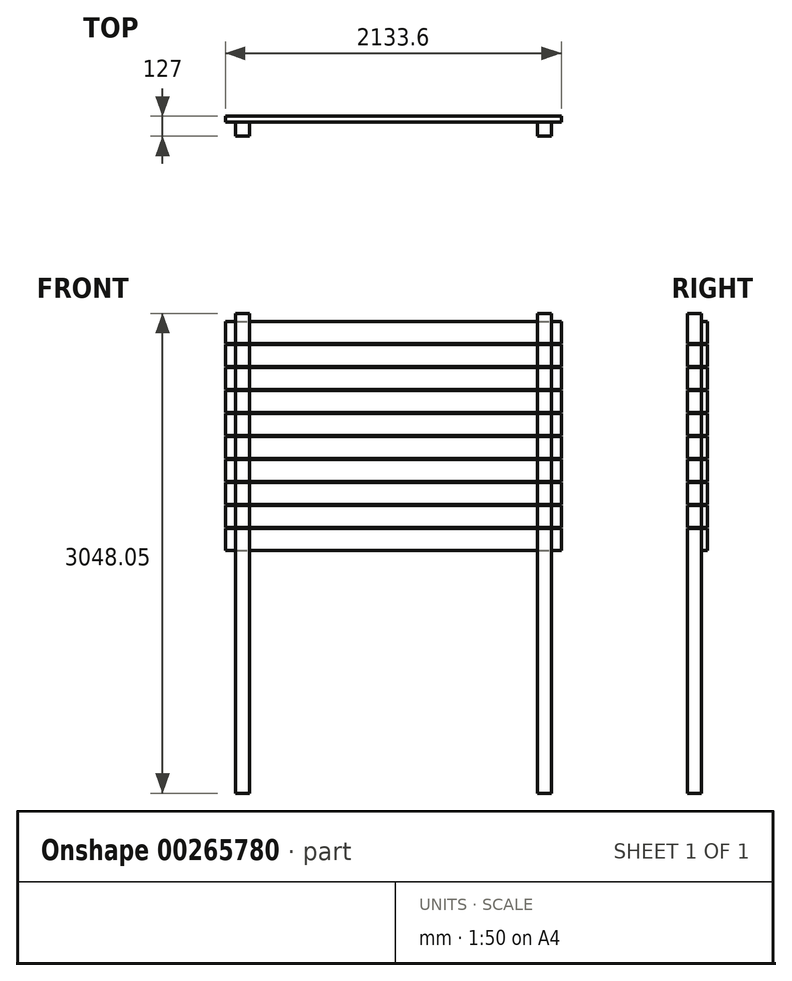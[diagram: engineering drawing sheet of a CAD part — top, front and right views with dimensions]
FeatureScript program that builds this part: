
annotation { "Feature Type Name" : "Feature", "Feature Type Description" : "" }
export const myFeature = defineFeature(function(context is Context, id is Id, definition is map)
    precondition{}
    {
        {
            var Q0;
            Q0=qCreatedBy(makeId("Front.planeOp"),FACE);
            var sketch = newSketch(context, id + "F0", { "sketchPlane" : qUnion([Q0])});
            skLineSegment(sketch, "E0.bottom", {"start": v(-158.67, 1590.1) * mm, "end": v(-69.77, 1590.1) * mm});
            skLineSegment(sketch, "E0.top", {"start": v(-158.67, -1457.9) * mm, "end": v(-69.77, -1457.9) * mm});
            skLineSegment(sketch, "E0.left", {"start": v(-158.67, 1590.1) * mm, "end": v(-158.67, -1457.9) * mm});
            skLineSegment(sketch, "E0.right", {"start": v(-69.77, 1590.1) * mm, "end": v(-69.77, -1457.9) * mm});
            skLineSegment(sketch, "E1.bottom", {"start": v(1759.03, 1590.04) * mm, "end": v(1847.93, 1590.04) * mm});
            skLineSegment(sketch, "E1.top", {"start": v(1759.03, -1457.96) * mm, "end": v(1847.93, -1457.96) * mm});
            skLineSegment(sketch, "E1.left", {"start": v(1759.03, 1590.04) * mm, "end": v(1759.03, -1457.96) * mm});
            skLineSegment(sketch, "E1.right", {"start": v(1847.93, 1590.04) * mm, "end": v(1847.93, -1457.96) * mm});
            skLineSegment(sketch, "E2", {"start": v(-615.63, -543.5) * mm, "end": v(2237.65, -543.5) * mm});
            skLineSegment(sketch, "E3.bottom", {"start": v(-222.17, 1539.46) * mm, "end": v(1911.43, 1539.46) * mm});
            skLineSegment(sketch, "E3.top", {"start": v(-222.17, 1399.76) * mm, "end": v(1911.43, 1399.76) * mm});
            skLineSegment(sketch, "E3.left", {"start": v(-222.17, 1539.46) * mm, "end": v(-222.17, 1399.76) * mm});
            skLineSegment(sketch, "E3.right", {"start": v(1911.43, 1539.46) * mm, "end": v(1911.43, 1399.76) * mm});
            skLineSegment(sketch, "E4.0.1.0", {"start": v(-222.17, 1393.41) * mm, "end": v(-222.17, 1253.71) * mm});
            skLineSegment(sketch, "E4.0.1.1", {"start": v(-222.17, 1393.41) * mm, "end": v(1911.43, 1393.41) * mm});
            skLineSegment(sketch, "E4.0.1.2", {"start": v(-222.17, 1253.71) * mm, "end": v(1911.43, 1253.71) * mm});
            skLineSegment(sketch, "E4.0.1.3", {"start": v(1911.43, 1393.41) * mm, "end": v(1911.43, 1253.71) * mm});
            skLineSegment(sketch, "E4.0.2.0", {"start": v(-222.17, 1247.36) * mm, "end": v(-222.17, 1107.66) * mm});
            skLineSegment(sketch, "E4.0.2.1", {"start": v(-222.17, 1247.36) * mm, "end": v(1911.43, 1247.36) * mm});
            skLineSegment(sketch, "E4.0.2.2", {"start": v(-222.17, 1107.66) * mm, "end": v(1911.43, 1107.66) * mm});
            skLineSegment(sketch, "E4.0.2.3", {"start": v(1911.43, 1247.36) * mm, "end": v(1911.43, 1107.66) * mm});
            skLineSegment(sketch, "E4.0.3.0", {"start": v(-222.17, 1101.31) * mm, "end": v(-222.17, 961.61) * mm});
            skLineSegment(sketch, "E4.0.3.1", {"start": v(-222.17, 1101.31) * mm, "end": v(1911.43, 1101.31) * mm});
            skLineSegment(sketch, "E4.0.3.2", {"start": v(-222.17, 961.61) * mm, "end": v(1911.43, 961.61) * mm});
            skLineSegment(sketch, "E4.0.3.3", {"start": v(1911.43, 1101.31) * mm, "end": v(1911.43, 961.61) * mm});
            skLineSegment(sketch, "E4.0.4.0", {"start": v(-222.17, 955.26) * mm, "end": v(-222.17, 815.56) * mm});
            skLineSegment(sketch, "E4.0.4.1", {"start": v(-222.17, 955.26) * mm, "end": v(1911.43, 955.26) * mm});
            skLineSegment(sketch, "E4.0.4.2", {"start": v(-222.17, 815.56) * mm, "end": v(1911.43, 815.56) * mm});
            skLineSegment(sketch, "E4.0.4.3", {"start": v(1911.43, 955.26) * mm, "end": v(1911.43, 815.56) * mm});
            skLineSegment(sketch, "E4.0.5.0", {"start": v(-222.17, 809.21) * mm, "end": v(-222.17, 669.51) * mm});
            skLineSegment(sketch, "E4.0.5.1", {"start": v(-222.17, 809.21) * mm, "end": v(1911.43, 809.21) * mm});
            skLineSegment(sketch, "E4.0.5.2", {"start": v(-222.17, 669.51) * mm, "end": v(1911.43, 669.51) * mm});
            skLineSegment(sketch, "E4.0.5.3", {"start": v(1911.43, 809.21) * mm, "end": v(1911.43, 669.51) * mm});
            skLineSegment(sketch, "E4.0.6.0", {"start": v(-222.17, 663.16) * mm, "end": v(-222.17, 523.46) * mm});
            skLineSegment(sketch, "E4.0.6.1", {"start": v(-222.17, 663.16) * mm, "end": v(1911.43, 663.16) * mm});
            skLineSegment(sketch, "E4.0.6.2", {"start": v(-222.17, 523.46) * mm, "end": v(1911.43, 523.46) * mm});
            skLineSegment(sketch, "E4.0.6.3", {"start": v(1911.43, 663.16) * mm, "end": v(1911.43, 523.46) * mm});
            skLineSegment(sketch, "E4.0.7.0", {"start": v(-222.17, 517.11) * mm, "end": v(-222.17, 377.41) * mm});
            skLineSegment(sketch, "E4.0.7.1", {"start": v(-222.17, 517.11) * mm, "end": v(1911.43, 517.11) * mm});
            skLineSegment(sketch, "E4.0.7.2", {"start": v(-222.17, 377.41) * mm, "end": v(1911.43, 377.41) * mm});
            skLineSegment(sketch, "E4.0.7.3", {"start": v(1911.43, 517.11) * mm, "end": v(1911.43, 377.41) * mm});
            skLineSegment(sketch, "E4.0.8.0", {"start": v(-222.17, 371.06) * mm, "end": v(-222.17, 231.36) * mm});
            skLineSegment(sketch, "E4.0.8.1", {"start": v(-222.17, 371.06) * mm, "end": v(1911.43, 371.06) * mm});
            skLineSegment(sketch, "E4.0.8.2", {"start": v(-222.17, 231.36) * mm, "end": v(1911.43, 231.36) * mm});
            skLineSegment(sketch, "E4.0.8.3", {"start": v(1911.43, 371.06) * mm, "end": v(1911.43, 231.36) * mm});
            skLineSegment(sketch, "E4.0.9.0", {"start": v(-222.17, 225.01) * mm, "end": v(-222.17, 85.31) * mm});
            skLineSegment(sketch, "E4.0.9.1", {"start": v(-222.17, 225.01) * mm, "end": v(1911.43, 225.01) * mm});
            skLineSegment(sketch, "E4.0.9.2", {"start": v(-222.17, 85.31) * mm, "end": v(1911.43, 85.31) * mm});
            skLineSegment(sketch, "E4.0.9.3", {"start": v(1911.43, 225.01) * mm, "end": v(1911.43, 85.31) * mm});
            skLineSegment(sketch, "E4.direction1", {"start": v(-222.17, 1399.76) * mm, "end": v(-219.63, 1399.76) * mm, "construction": true});
            skLineSegment(sketch, "E4.direction2", {"start": v(-222.17, 1399.76) * mm, "end": v(-222.17, 1253.71) * mm, "construction": true});
            skSolve(sketch);
        }
        {
            var Q0;
            {var subQ0=sQuery(id+"F0.wireOp",EDGE,"E0.top");Q0=makeQuery(id+"F0.imprint","IMPRINT",FACE,{"disambiguationData":[TD([[makeQuery(id+"F0.imprint","IMPRINT",EDGE,{"derivedFrom":subQ0}),1.0]])]});}
            var Q1;
            {var subQ0=sQuery(id+"F0.wireOp",EDGE,"E2");var subQ1=sQuery(id+"F0.wireOp",EDGE,"E0.left");var subQ2=makeQuery(id+"F0.imprint","INTERSECT",VERTEX,{"derivedFrom":[subQ1,subQ0]});Q1=makeQuery(id+"F0.imprint","IMPRINT",FACE,{"disambiguationData":[TD([[makeQuery(id+"F0.imprint","IMPRINT",EDGE,{"disambiguationData":[TD([[subQ2,1.0]])],"derivedFrom":subQ1}),1.0]])]});}
            var Q2;
            {var subQ0=sQuery(id+"F0.wireOp",EDGE,"E4.0.9.1");var subQ1=sQuery(id+"F0.wireOp",EDGE,"E0.left");var subQ2=makeQuery(id+"F0.imprint","INTERSECT",VERTEX,{"derivedFrom":[subQ1,subQ0]});Q2=makeQuery(id+"F0.imprint","IMPRINT",FACE,{"disambiguationData":[TD([[makeQuery(id+"F0.imprint","IMPRINT",EDGE,{"disambiguationData":[TD([[subQ2,-1.0]])],"derivedFrom":subQ1}),1.0]])]});}
            var Q3;
            {var subQ0=sQuery(id+"F0.wireOp",EDGE,"E4.0.8.1");var subQ1=sQuery(id+"F0.wireOp",EDGE,"E0.left");var subQ2=makeQuery(id+"F0.imprint","INTERSECT",VERTEX,{"derivedFrom":[subQ1,subQ0]});Q3=makeQuery(id+"F0.imprint","IMPRINT",FACE,{"disambiguationData":[TD([[makeQuery(id+"F0.imprint","IMPRINT",EDGE,{"disambiguationData":[TD([[subQ2,-1.0]])],"derivedFrom":subQ1}),1.0]])]});}
            var Q4;
            {var subQ0=sQuery(id+"F0.wireOp",EDGE,"E4.0.7.1");var subQ1=sQuery(id+"F0.wireOp",EDGE,"E0.left");var subQ2=makeQuery(id+"F0.imprint","INTERSECT",VERTEX,{"derivedFrom":[subQ1,subQ0]});Q4=makeQuery(id+"F0.imprint","IMPRINT",FACE,{"disambiguationData":[TD([[makeQuery(id+"F0.imprint","IMPRINT",EDGE,{"disambiguationData":[TD([[subQ2,-1.0]])],"derivedFrom":subQ1}),1.0]])]});}
            var Q5;
            {var subQ0=sQuery(id+"F0.wireOp",EDGE,"E4.0.6.1");var subQ1=sQuery(id+"F0.wireOp",EDGE,"E0.left");var subQ2=makeQuery(id+"F0.imprint","INTERSECT",VERTEX,{"derivedFrom":[subQ1,subQ0]});Q5=makeQuery(id+"F0.imprint","IMPRINT",FACE,{"disambiguationData":[TD([[makeQuery(id+"F0.imprint","IMPRINT",EDGE,{"disambiguationData":[TD([[subQ2,-1.0]])],"derivedFrom":subQ1}),1.0]])]});}
            var Q6;
            {var subQ0=sQuery(id+"F0.wireOp",EDGE,"E4.0.5.1");var subQ1=sQuery(id+"F0.wireOp",EDGE,"E0.left");var subQ2=makeQuery(id+"F0.imprint","INTERSECT",VERTEX,{"derivedFrom":[subQ1,subQ0]});Q6=makeQuery(id+"F0.imprint","IMPRINT",FACE,{"disambiguationData":[TD([[makeQuery(id+"F0.imprint","IMPRINT",EDGE,{"disambiguationData":[TD([[subQ2,-1.0]])],"derivedFrom":subQ1}),1.0]])]});}
            var Q7;
            {var subQ0=sQuery(id+"F0.wireOp",EDGE,"E4.0.4.1");var subQ1=sQuery(id+"F0.wireOp",EDGE,"E0.left");var subQ2=makeQuery(id+"F0.imprint","INTERSECT",VERTEX,{"derivedFrom":[subQ1,subQ0]});Q7=makeQuery(id+"F0.imprint","IMPRINT",FACE,{"disambiguationData":[TD([[makeQuery(id+"F0.imprint","IMPRINT",EDGE,{"disambiguationData":[TD([[subQ2,-1.0]])],"derivedFrom":subQ1}),1.0]])]});}
            var Q8;
            {var subQ0=sQuery(id+"F0.wireOp",EDGE,"E4.0.3.1");var subQ1=sQuery(id+"F0.wireOp",EDGE,"E0.left");var subQ2=makeQuery(id+"F0.imprint","INTERSECT",VERTEX,{"derivedFrom":[subQ1,subQ0]});Q8=makeQuery(id+"F0.imprint","IMPRINT",FACE,{"disambiguationData":[TD([[makeQuery(id+"F0.imprint","IMPRINT",EDGE,{"disambiguationData":[TD([[subQ2,-1.0]])],"derivedFrom":subQ1}),1.0]])]});}
            var Q9;
            {var subQ0=sQuery(id+"F0.wireOp",EDGE,"E4.0.2.1");var subQ1=sQuery(id+"F0.wireOp",EDGE,"E0.left");var subQ2=makeQuery(id+"F0.imprint","INTERSECT",VERTEX,{"derivedFrom":[subQ1,subQ0]});Q9=makeQuery(id+"F0.imprint","IMPRINT",FACE,{"disambiguationData":[TD([[makeQuery(id+"F0.imprint","IMPRINT",EDGE,{"disambiguationData":[TD([[subQ2,-1.0]])],"derivedFrom":subQ1}),1.0]])]});}
            var Q10;
            {var subQ0=sQuery(id+"F0.wireOp",EDGE,"E4.0.1.1");var subQ1=sQuery(id+"F0.wireOp",EDGE,"E0.left");var subQ2=makeQuery(id+"F0.imprint","INTERSECT",VERTEX,{"derivedFrom":[subQ1,subQ0]});Q10=makeQuery(id+"F0.imprint","IMPRINT",FACE,{"disambiguationData":[TD([[makeQuery(id+"F0.imprint","IMPRINT",EDGE,{"disambiguationData":[TD([[subQ2,-1.0]])],"derivedFrom":subQ1}),1.0]])]});}
            var Q11;
            {var subQ0=sQuery(id+"F0.wireOp",EDGE,"E3.bottom");var subQ1=sQuery(id+"F0.wireOp",EDGE,"E0.left");var subQ2=makeQuery(id+"F0.imprint","INTERSECT",VERTEX,{"derivedFrom":[subQ1,subQ0]});Q11=makeQuery(id+"F0.imprint","IMPRINT",FACE,{"disambiguationData":[TD([[makeQuery(id+"F0.imprint","IMPRINT",EDGE,{"disambiguationData":[TD([[subQ2,-1.0]])],"derivedFrom":subQ1}),1.0]])]});}
            var Q12;
            {var subQ0=sQuery(id+"F0.wireOp",EDGE,"E0.bottom");Q12=makeQuery(id+"F0.imprint","IMPRINT",FACE,{"disambiguationData":[TD([[makeQuery(id+"F0.imprint","IMPRINT",EDGE,{"derivedFrom":subQ0}),-1.0]])]});}
            var Q13;
            {var subQ0=sQuery(id+"F0.wireOp",EDGE,"E1.bottom");Q13=makeQuery(id+"F0.imprint","IMPRINT",FACE,{"disambiguationData":[TD([[makeQuery(id+"F0.imprint","IMPRINT",EDGE,{"derivedFrom":subQ0}),-1.0]])]});}
            var Q14;
            {var subQ0=sQuery(id+"F0.wireOp",EDGE,"E3.bottom");var subQ1=sQuery(id+"F0.wireOp",EDGE,"E1.left");var subQ2=makeQuery(id+"F0.imprint","INTERSECT",VERTEX,{"derivedFrom":[subQ1,subQ0]});Q14=makeQuery(id+"F0.imprint","IMPRINT",FACE,{"disambiguationData":[TD([[makeQuery(id+"F0.imprint","IMPRINT",EDGE,{"disambiguationData":[TD([[subQ2,-1.0]])],"derivedFrom":subQ1}),1.0]])]});}
            var Q15;
            {var subQ0=sQuery(id+"F0.wireOp",EDGE,"E4.0.1.1");var subQ1=sQuery(id+"F0.wireOp",EDGE,"E1.left");var subQ2=makeQuery(id+"F0.imprint","INTERSECT",VERTEX,{"derivedFrom":[subQ1,subQ0]});Q15=makeQuery(id+"F0.imprint","IMPRINT",FACE,{"disambiguationData":[TD([[makeQuery(id+"F0.imprint","IMPRINT",EDGE,{"disambiguationData":[TD([[subQ2,-1.0]])],"derivedFrom":subQ1}),1.0]])]});}
            var Q16;
            {var subQ0=sQuery(id+"F0.wireOp",EDGE,"E4.0.2.1");var subQ1=sQuery(id+"F0.wireOp",EDGE,"E1.left");var subQ2=makeQuery(id+"F0.imprint","INTERSECT",VERTEX,{"derivedFrom":[subQ1,subQ0]});Q16=makeQuery(id+"F0.imprint","IMPRINT",FACE,{"disambiguationData":[TD([[makeQuery(id+"F0.imprint","IMPRINT",EDGE,{"disambiguationData":[TD([[subQ2,-1.0]])],"derivedFrom":subQ1}),1.0]])]});}
            var Q17;
            {var subQ0=sQuery(id+"F0.wireOp",EDGE,"E4.0.3.1");var subQ1=sQuery(id+"F0.wireOp",EDGE,"E1.left");var subQ2=makeQuery(id+"F0.imprint","INTERSECT",VERTEX,{"derivedFrom":[subQ1,subQ0]});Q17=makeQuery(id+"F0.imprint","IMPRINT",FACE,{"disambiguationData":[TD([[makeQuery(id+"F0.imprint","IMPRINT",EDGE,{"disambiguationData":[TD([[subQ2,-1.0]])],"derivedFrom":subQ1}),1.0]])]});}
            var Q18;
            {var subQ0=sQuery(id+"F0.wireOp",EDGE,"E4.0.4.1");var subQ1=sQuery(id+"F0.wireOp",EDGE,"E1.left");var subQ2=makeQuery(id+"F0.imprint","INTERSECT",VERTEX,{"derivedFrom":[subQ1,subQ0]});Q18=makeQuery(id+"F0.imprint","IMPRINT",FACE,{"disambiguationData":[TD([[makeQuery(id+"F0.imprint","IMPRINT",EDGE,{"disambiguationData":[TD([[subQ2,-1.0]])],"derivedFrom":subQ1}),1.0]])]});}
            var Q19;
            {var subQ0=sQuery(id+"F0.wireOp",EDGE,"E4.0.5.1");var subQ1=sQuery(id+"F0.wireOp",EDGE,"E1.left");var subQ2=makeQuery(id+"F0.imprint","INTERSECT",VERTEX,{"derivedFrom":[subQ1,subQ0]});Q19=makeQuery(id+"F0.imprint","IMPRINT",FACE,{"disambiguationData":[TD([[makeQuery(id+"F0.imprint","IMPRINT",EDGE,{"disambiguationData":[TD([[subQ2,-1.0]])],"derivedFrom":subQ1}),1.0]])]});}
            var Q20;
            {var subQ0=sQuery(id+"F0.wireOp",EDGE,"E4.0.6.1");var subQ1=sQuery(id+"F0.wireOp",EDGE,"E1.left");var subQ2=makeQuery(id+"F0.imprint","INTERSECT",VERTEX,{"derivedFrom":[subQ1,subQ0]});Q20=makeQuery(id+"F0.imprint","IMPRINT",FACE,{"disambiguationData":[TD([[makeQuery(id+"F0.imprint","IMPRINT",EDGE,{"disambiguationData":[TD([[subQ2,-1.0]])],"derivedFrom":subQ1}),1.0]])]});}
            var Q21;
            {var subQ0=sQuery(id+"F0.wireOp",EDGE,"E4.0.7.1");var subQ1=sQuery(id+"F0.wireOp",EDGE,"E1.left");var subQ2=makeQuery(id+"F0.imprint","INTERSECT",VERTEX,{"derivedFrom":[subQ1,subQ0]});Q21=makeQuery(id+"F0.imprint","IMPRINT",FACE,{"disambiguationData":[TD([[makeQuery(id+"F0.imprint","IMPRINT",EDGE,{"disambiguationData":[TD([[subQ2,-1.0]])],"derivedFrom":subQ1}),1.0]])]});}
            var Q22;
            {var subQ0=sQuery(id+"F0.wireOp",EDGE,"E4.0.8.1");var subQ1=sQuery(id+"F0.wireOp",EDGE,"E1.left");var subQ2=makeQuery(id+"F0.imprint","INTERSECT",VERTEX,{"derivedFrom":[subQ1,subQ0]});Q22=makeQuery(id+"F0.imprint","IMPRINT",FACE,{"disambiguationData":[TD([[makeQuery(id+"F0.imprint","IMPRINT",EDGE,{"disambiguationData":[TD([[subQ2,-1.0]])],"derivedFrom":subQ1}),1.0]])]});}
            var Q23;
            {var subQ0=sQuery(id+"F0.wireOp",EDGE,"E4.0.9.1");var subQ1=sQuery(id+"F0.wireOp",EDGE,"E1.left");var subQ2=makeQuery(id+"F0.imprint","INTERSECT",VERTEX,{"derivedFrom":[subQ1,subQ0]});Q23=makeQuery(id+"F0.imprint","IMPRINT",FACE,{"disambiguationData":[TD([[makeQuery(id+"F0.imprint","IMPRINT",EDGE,{"disambiguationData":[TD([[subQ2,-1.0]])],"derivedFrom":subQ1}),1.0]])]});}
            var Q24;
            {var subQ0=sQuery(id+"F0.wireOp",EDGE,"E2");var subQ1=sQuery(id+"F0.wireOp",EDGE,"E1.left");var subQ2=makeQuery(id+"F0.imprint","INTERSECT",VERTEX,{"derivedFrom":[subQ1,subQ0]});Q24=makeQuery(id+"F0.imprint","IMPRINT",FACE,{"disambiguationData":[TD([[makeQuery(id+"F0.imprint","IMPRINT",EDGE,{"disambiguationData":[TD([[subQ2,1.0]])],"derivedFrom":subQ1}),1.0]])]});}
            var Q25;
            {var subQ0=sQuery(id+"F0.wireOp",EDGE,"E1.top");Q25=makeQuery(id+"F0.imprint","IMPRINT",FACE,{"disambiguationData":[TD([[makeQuery(id+"F0.imprint","IMPRINT",EDGE,{"derivedFrom":subQ0}),1.0]])]});}
            extrude(context, id + "F1", {"entities" : qUnion([Q0, Q1, Q2, Q3, Q4, Q5, Q6, Q7, Q8, Q9, Q10, Q11, Q12, Q13, Q14, Q15, Q16, Q17, Q18, Q19, Q20, Q21, Q22, Q23, Q24, Q25]), "depth" : 88.9 * mm});
        }
        {
            var Q0;
            {var subQ5=sQuery(id+"F0.wireOp",EDGE,"E3.left");Q0=makeQuery(id+"F0.imprint","IMPRINT",FACE,{"disambiguationData":[TD([[makeQuery(id+"F0.imprint","IMPRINT",EDGE,{"derivedFrom":subQ5}),1.0]])]});}
            var Q1;
            {var subQ0=sQuery(id+"F0.wireOp",EDGE,"E3.bottom");var subQ1=sQuery(id+"F0.wireOp",EDGE,"E0.right");var subQ2=makeQuery(id+"F0.imprint","INTERSECT",VERTEX,{"derivedFrom":[subQ1,subQ0]});Q1=makeQuery(id+"F0.imprint","IMPRINT",FACE,{"disambiguationData":[TD([[makeQuery(id+"F0.imprint","IMPRINT",EDGE,{"disambiguationData":[TD([[subQ2,-1.0]])],"derivedFrom":subQ1}),1.0]])]});}
            var Q2;
            {var subQ0=sQuery(id+"F0.wireOp",EDGE,"E3.bottom");var subQ1=sQuery(id+"F0.wireOp",EDGE,"E0.left");var subQ2=makeQuery(id+"F0.imprint","INTERSECT",VERTEX,{"derivedFrom":[subQ1,subQ0]});Q2=makeQuery(id+"F0.imprint","IMPRINT",FACE,{"disambiguationData":[TD([[makeQuery(id+"F0.imprint","IMPRINT",EDGE,{"disambiguationData":[TD([[subQ2,-1.0]])],"derivedFrom":subQ1}),1.0]])]});}
            var Q3;
            {var subQ5=sQuery(id+"F0.wireOp",EDGE,"E4.0.1.0");Q3=makeQuery(id+"F0.imprint","IMPRINT",FACE,{"disambiguationData":[TD([[makeQuery(id+"F0.imprint","IMPRINT",EDGE,{"derivedFrom":subQ5}),1.0]])]});}
            var Q4;
            {var subQ0=sQuery(id+"F0.wireOp",EDGE,"E4.0.1.1");var subQ1=sQuery(id+"F0.wireOp",EDGE,"E0.left");var subQ2=makeQuery(id+"F0.imprint","INTERSECT",VERTEX,{"derivedFrom":[subQ1,subQ0]});Q4=makeQuery(id+"F0.imprint","IMPRINT",FACE,{"disambiguationData":[TD([[makeQuery(id+"F0.imprint","IMPRINT",EDGE,{"disambiguationData":[TD([[subQ2,-1.0]])],"derivedFrom":subQ1}),1.0]])]});}
            var Q5;
            {var subQ0=sQuery(id+"F0.wireOp",EDGE,"E4.0.1.1");var subQ1=sQuery(id+"F0.wireOp",EDGE,"E0.right");var subQ2=makeQuery(id+"F0.imprint","INTERSECT",VERTEX,{"derivedFrom":[subQ1,subQ0]});Q5=makeQuery(id+"F0.imprint","IMPRINT",FACE,{"disambiguationData":[TD([[makeQuery(id+"F0.imprint","IMPRINT",EDGE,{"disambiguationData":[TD([[subQ2,-1.0]])],"derivedFrom":subQ1}),1.0]])]});}
            var Q6;
            {var subQ5=sQuery(id+"F0.wireOp",EDGE,"E4.0.2.0");Q6=makeQuery(id+"F0.imprint","IMPRINT",FACE,{"disambiguationData":[TD([[makeQuery(id+"F0.imprint","IMPRINT",EDGE,{"derivedFrom":subQ5}),1.0]])]});}
            var Q7;
            {var subQ0=sQuery(id+"F0.wireOp",EDGE,"E4.0.2.1");var subQ1=sQuery(id+"F0.wireOp",EDGE,"E0.left");var subQ2=makeQuery(id+"F0.imprint","INTERSECT",VERTEX,{"derivedFrom":[subQ1,subQ0]});Q7=makeQuery(id+"F0.imprint","IMPRINT",FACE,{"disambiguationData":[TD([[makeQuery(id+"F0.imprint","IMPRINT",EDGE,{"disambiguationData":[TD([[subQ2,-1.0]])],"derivedFrom":subQ1}),1.0]])]});}
            var Q8;
            {var subQ0=sQuery(id+"F0.wireOp",EDGE,"E4.0.2.1");var subQ1=sQuery(id+"F0.wireOp",EDGE,"E0.right");var subQ2=makeQuery(id+"F0.imprint","INTERSECT",VERTEX,{"derivedFrom":[subQ1,subQ0]});Q8=makeQuery(id+"F0.imprint","IMPRINT",FACE,{"disambiguationData":[TD([[makeQuery(id+"F0.imprint","IMPRINT",EDGE,{"disambiguationData":[TD([[subQ2,-1.0]])],"derivedFrom":subQ1}),1.0]])]});}
            var Q9;
            {var subQ5=sQuery(id+"F0.wireOp",EDGE,"E4.0.3.0");Q9=makeQuery(id+"F0.imprint","IMPRINT",FACE,{"disambiguationData":[TD([[makeQuery(id+"F0.imprint","IMPRINT",EDGE,{"derivedFrom":subQ5}),1.0]])]});}
            var Q10;
            {var subQ0=sQuery(id+"F0.wireOp",EDGE,"E4.0.3.1");var subQ1=sQuery(id+"F0.wireOp",EDGE,"E0.left");var subQ2=makeQuery(id+"F0.imprint","INTERSECT",VERTEX,{"derivedFrom":[subQ1,subQ0]});Q10=makeQuery(id+"F0.imprint","IMPRINT",FACE,{"disambiguationData":[TD([[makeQuery(id+"F0.imprint","IMPRINT",EDGE,{"disambiguationData":[TD([[subQ2,-1.0]])],"derivedFrom":subQ1}),1.0]])]});}
            var Q11;
            {var subQ0=sQuery(id+"F0.wireOp",EDGE,"E4.0.3.1");var subQ1=sQuery(id+"F0.wireOp",EDGE,"E0.right");var subQ2=makeQuery(id+"F0.imprint","INTERSECT",VERTEX,{"derivedFrom":[subQ1,subQ0]});Q11=makeQuery(id+"F0.imprint","IMPRINT",FACE,{"disambiguationData":[TD([[makeQuery(id+"F0.imprint","IMPRINT",EDGE,{"disambiguationData":[TD([[subQ2,-1.0]])],"derivedFrom":subQ1}),1.0]])]});}
            var Q12;
            {var subQ5=sQuery(id+"F0.wireOp",EDGE,"E4.0.4.0");Q12=makeQuery(id+"F0.imprint","IMPRINT",FACE,{"disambiguationData":[TD([[makeQuery(id+"F0.imprint","IMPRINT",EDGE,{"derivedFrom":subQ5}),1.0]])]});}
            var Q13;
            {var subQ0=sQuery(id+"F0.wireOp",EDGE,"E4.0.4.1");var subQ1=sQuery(id+"F0.wireOp",EDGE,"E0.left");var subQ2=makeQuery(id+"F0.imprint","INTERSECT",VERTEX,{"derivedFrom":[subQ1,subQ0]});Q13=makeQuery(id+"F0.imprint","IMPRINT",FACE,{"disambiguationData":[TD([[makeQuery(id+"F0.imprint","IMPRINT",EDGE,{"disambiguationData":[TD([[subQ2,-1.0]])],"derivedFrom":subQ1}),1.0]])]});}
            var Q14;
            {var subQ0=sQuery(id+"F0.wireOp",EDGE,"E4.0.4.1");var subQ1=sQuery(id+"F0.wireOp",EDGE,"E0.right");var subQ2=makeQuery(id+"F0.imprint","INTERSECT",VERTEX,{"derivedFrom":[subQ1,subQ0]});Q14=makeQuery(id+"F0.imprint","IMPRINT",FACE,{"disambiguationData":[TD([[makeQuery(id+"F0.imprint","IMPRINT",EDGE,{"disambiguationData":[TD([[subQ2,-1.0]])],"derivedFrom":subQ1}),1.0]])]});}
            var Q15;
            {var subQ5=sQuery(id+"F0.wireOp",EDGE,"E4.0.5.0");Q15=makeQuery(id+"F0.imprint","IMPRINT",FACE,{"disambiguationData":[TD([[makeQuery(id+"F0.imprint","IMPRINT",EDGE,{"derivedFrom":subQ5}),1.0]])]});}
            var Q16;
            {var subQ0=sQuery(id+"F0.wireOp",EDGE,"E4.0.5.1");var subQ1=sQuery(id+"F0.wireOp",EDGE,"E0.left");var subQ2=makeQuery(id+"F0.imprint","INTERSECT",VERTEX,{"derivedFrom":[subQ1,subQ0]});Q16=makeQuery(id+"F0.imprint","IMPRINT",FACE,{"disambiguationData":[TD([[makeQuery(id+"F0.imprint","IMPRINT",EDGE,{"disambiguationData":[TD([[subQ2,-1.0]])],"derivedFrom":subQ1}),1.0]])]});}
            var Q17;
            {var subQ0=sQuery(id+"F0.wireOp",EDGE,"E4.0.5.1");var subQ1=sQuery(id+"F0.wireOp",EDGE,"E0.right");var subQ2=makeQuery(id+"F0.imprint","INTERSECT",VERTEX,{"derivedFrom":[subQ1,subQ0]});Q17=makeQuery(id+"F0.imprint","IMPRINT",FACE,{"disambiguationData":[TD([[makeQuery(id+"F0.imprint","IMPRINT",EDGE,{"disambiguationData":[TD([[subQ2,-1.0]])],"derivedFrom":subQ1}),1.0]])]});}
            var Q18;
            {var subQ5=sQuery(id+"F0.wireOp",EDGE,"E4.0.6.0");Q18=makeQuery(id+"F0.imprint","IMPRINT",FACE,{"disambiguationData":[TD([[makeQuery(id+"F0.imprint","IMPRINT",EDGE,{"derivedFrom":subQ5}),1.0]])]});}
            var Q19;
            {var subQ0=sQuery(id+"F0.wireOp",EDGE,"E4.0.6.1");var subQ1=sQuery(id+"F0.wireOp",EDGE,"E0.right");var subQ2=makeQuery(id+"F0.imprint","INTERSECT",VERTEX,{"derivedFrom":[subQ1,subQ0]});Q19=makeQuery(id+"F0.imprint","IMPRINT",FACE,{"disambiguationData":[TD([[makeQuery(id+"F0.imprint","IMPRINT",EDGE,{"disambiguationData":[TD([[subQ2,-1.0]])],"derivedFrom":subQ1}),1.0]])]});}
            var Q20;
            {var subQ0=sQuery(id+"F0.wireOp",EDGE,"E4.0.6.1");var subQ1=sQuery(id+"F0.wireOp",EDGE,"E0.left");var subQ2=makeQuery(id+"F0.imprint","INTERSECT",VERTEX,{"derivedFrom":[subQ1,subQ0]});Q20=makeQuery(id+"F0.imprint","IMPRINT",FACE,{"disambiguationData":[TD([[makeQuery(id+"F0.imprint","IMPRINT",EDGE,{"disambiguationData":[TD([[subQ2,-1.0]])],"derivedFrom":subQ1}),1.0]])]});}
            var Q21;
            {var subQ5=sQuery(id+"F0.wireOp",EDGE,"E4.0.7.0");Q21=makeQuery(id+"F0.imprint","IMPRINT",FACE,{"disambiguationData":[TD([[makeQuery(id+"F0.imprint","IMPRINT",EDGE,{"derivedFrom":subQ5}),1.0]])]});}
            var Q22;
            {var subQ0=sQuery(id+"F0.wireOp",EDGE,"E4.0.7.1");var subQ1=sQuery(id+"F0.wireOp",EDGE,"E0.left");var subQ2=makeQuery(id+"F0.imprint","INTERSECT",VERTEX,{"derivedFrom":[subQ1,subQ0]});Q22=makeQuery(id+"F0.imprint","IMPRINT",FACE,{"disambiguationData":[TD([[makeQuery(id+"F0.imprint","IMPRINT",EDGE,{"disambiguationData":[TD([[subQ2,-1.0]])],"derivedFrom":subQ1}),1.0]])]});}
            var Q23;
            {var subQ0=sQuery(id+"F0.wireOp",EDGE,"E4.0.7.1");var subQ1=sQuery(id+"F0.wireOp",EDGE,"E0.right");var subQ2=makeQuery(id+"F0.imprint","INTERSECT",VERTEX,{"derivedFrom":[subQ1,subQ0]});Q23=makeQuery(id+"F0.imprint","IMPRINT",FACE,{"disambiguationData":[TD([[makeQuery(id+"F0.imprint","IMPRINT",EDGE,{"disambiguationData":[TD([[subQ2,-1.0]])],"derivedFrom":subQ1}),1.0]])]});}
            var Q24;
            {var subQ5=sQuery(id+"F0.wireOp",EDGE,"E4.0.8.0");Q24=makeQuery(id+"F0.imprint","IMPRINT",FACE,{"disambiguationData":[TD([[makeQuery(id+"F0.imprint","IMPRINT",EDGE,{"derivedFrom":subQ5}),1.0]])]});}
            var Q25;
            {var subQ0=sQuery(id+"F0.wireOp",EDGE,"E4.0.8.1");var subQ1=sQuery(id+"F0.wireOp",EDGE,"E0.left");var subQ2=makeQuery(id+"F0.imprint","INTERSECT",VERTEX,{"derivedFrom":[subQ1,subQ0]});Q25=makeQuery(id+"F0.imprint","IMPRINT",FACE,{"disambiguationData":[TD([[makeQuery(id+"F0.imprint","IMPRINT",EDGE,{"disambiguationData":[TD([[subQ2,-1.0]])],"derivedFrom":subQ1}),1.0]])]});}
            var Q26;
            {var subQ0=sQuery(id+"F0.wireOp",EDGE,"E4.0.8.1");var subQ1=sQuery(id+"F0.wireOp",EDGE,"E0.right");var subQ2=makeQuery(id+"F0.imprint","INTERSECT",VERTEX,{"derivedFrom":[subQ1,subQ0]});Q26=makeQuery(id+"F0.imprint","IMPRINT",FACE,{"disambiguationData":[TD([[makeQuery(id+"F0.imprint","IMPRINT",EDGE,{"disambiguationData":[TD([[subQ2,-1.0]])],"derivedFrom":subQ1}),1.0]])]});}
            var Q27;
            {var subQ5=sQuery(id+"F0.wireOp",EDGE,"E4.0.9.0");Q27=makeQuery(id+"F0.imprint","IMPRINT",FACE,{"disambiguationData":[TD([[makeQuery(id+"F0.imprint","IMPRINT",EDGE,{"derivedFrom":subQ5}),1.0]])]});}
            var Q28;
            {var subQ0=sQuery(id+"F0.wireOp",EDGE,"E4.0.9.1");var subQ1=sQuery(id+"F0.wireOp",EDGE,"E0.left");var subQ2=makeQuery(id+"F0.imprint","INTERSECT",VERTEX,{"derivedFrom":[subQ1,subQ0]});Q28=makeQuery(id+"F0.imprint","IMPRINT",FACE,{"disambiguationData":[TD([[makeQuery(id+"F0.imprint","IMPRINT",EDGE,{"disambiguationData":[TD([[subQ2,-1.0]])],"derivedFrom":subQ1}),1.0]])]});}
            var Q29;
            {var subQ0=sQuery(id+"F0.wireOp",EDGE,"E4.0.9.1");var subQ1=sQuery(id+"F0.wireOp",EDGE,"E0.right");var subQ2=makeQuery(id+"F0.imprint","INTERSECT",VERTEX,{"derivedFrom":[subQ1,subQ0]});Q29=makeQuery(id+"F0.imprint","IMPRINT",FACE,{"disambiguationData":[TD([[makeQuery(id+"F0.imprint","IMPRINT",EDGE,{"disambiguationData":[TD([[subQ2,-1.0]])],"derivedFrom":subQ1}),1.0]])]});}
            var Q30;
            {var subQ0=sQuery(id+"F0.wireOp",EDGE,"E4.0.9.1");var subQ1=sQuery(id+"F0.wireOp",EDGE,"E1.left");var subQ2=makeQuery(id+"F0.imprint","INTERSECT",VERTEX,{"derivedFrom":[subQ1,subQ0]});Q30=makeQuery(id+"F0.imprint","IMPRINT",FACE,{"disambiguationData":[TD([[makeQuery(id+"F0.imprint","IMPRINT",EDGE,{"disambiguationData":[TD([[subQ2,-1.0]])],"derivedFrom":subQ1}),1.0]])]});}
            var Q31;
            {var subQ5=sQuery(id+"F0.wireOp",EDGE,"E4.0.9.3");Q31=makeQuery(id+"F0.imprint","IMPRINT",FACE,{"disambiguationData":[TD([[makeQuery(id+"F0.imprint","IMPRINT",EDGE,{"derivedFrom":subQ5}),-1.0]])]});}
            var Q32;
            {var subQ0=sQuery(id+"F0.wireOp",EDGE,"E4.0.8.1");var subQ1=sQuery(id+"F0.wireOp",EDGE,"E1.left");var subQ2=makeQuery(id+"F0.imprint","INTERSECT",VERTEX,{"derivedFrom":[subQ1,subQ0]});Q32=makeQuery(id+"F0.imprint","IMPRINT",FACE,{"disambiguationData":[TD([[makeQuery(id+"F0.imprint","IMPRINT",EDGE,{"disambiguationData":[TD([[subQ2,-1.0]])],"derivedFrom":subQ1}),1.0]])]});}
            var Q33;
            {var subQ5=sQuery(id+"F0.wireOp",EDGE,"E4.0.8.3");Q33=makeQuery(id+"F0.imprint","IMPRINT",FACE,{"disambiguationData":[TD([[makeQuery(id+"F0.imprint","IMPRINT",EDGE,{"derivedFrom":subQ5}),-1.0]])]});}
            var Q34;
            {var subQ0=sQuery(id+"F0.wireOp",EDGE,"E4.0.7.1");var subQ1=sQuery(id+"F0.wireOp",EDGE,"E1.left");var subQ2=makeQuery(id+"F0.imprint","INTERSECT",VERTEX,{"derivedFrom":[subQ1,subQ0]});Q34=makeQuery(id+"F0.imprint","IMPRINT",FACE,{"disambiguationData":[TD([[makeQuery(id+"F0.imprint","IMPRINT",EDGE,{"disambiguationData":[TD([[subQ2,-1.0]])],"derivedFrom":subQ1}),1.0]])]});}
            var Q35;
            {var subQ5=sQuery(id+"F0.wireOp",EDGE,"E4.0.7.3");Q35=makeQuery(id+"F0.imprint","IMPRINT",FACE,{"disambiguationData":[TD([[makeQuery(id+"F0.imprint","IMPRINT",EDGE,{"derivedFrom":subQ5}),-1.0]])]});}
            var Q36;
            {var subQ0=sQuery(id+"F0.wireOp",EDGE,"E4.0.6.1");var subQ1=sQuery(id+"F0.wireOp",EDGE,"E1.left");var subQ2=makeQuery(id+"F0.imprint","INTERSECT",VERTEX,{"derivedFrom":[subQ1,subQ0]});Q36=makeQuery(id+"F0.imprint","IMPRINT",FACE,{"disambiguationData":[TD([[makeQuery(id+"F0.imprint","IMPRINT",EDGE,{"disambiguationData":[TD([[subQ2,-1.0]])],"derivedFrom":subQ1}),1.0]])]});}
            var Q37;
            {var subQ5=sQuery(id+"F0.wireOp",EDGE,"E4.0.6.3");Q37=makeQuery(id+"F0.imprint","IMPRINT",FACE,{"disambiguationData":[TD([[makeQuery(id+"F0.imprint","IMPRINT",EDGE,{"derivedFrom":subQ5}),-1.0]])]});}
            var Q38;
            {var subQ0=sQuery(id+"F0.wireOp",EDGE,"E4.0.5.1");var subQ1=sQuery(id+"F0.wireOp",EDGE,"E1.left");var subQ2=makeQuery(id+"F0.imprint","INTERSECT",VERTEX,{"derivedFrom":[subQ1,subQ0]});Q38=makeQuery(id+"F0.imprint","IMPRINT",FACE,{"disambiguationData":[TD([[makeQuery(id+"F0.imprint","IMPRINT",EDGE,{"disambiguationData":[TD([[subQ2,-1.0]])],"derivedFrom":subQ1}),1.0]])]});}
            var Q39;
            {var subQ5=sQuery(id+"F0.wireOp",EDGE,"E4.0.5.3");Q39=makeQuery(id+"F0.imprint","IMPRINT",FACE,{"disambiguationData":[TD([[makeQuery(id+"F0.imprint","IMPRINT",EDGE,{"derivedFrom":subQ5}),-1.0]])]});}
            var Q40;
            {var subQ0=sQuery(id+"F0.wireOp",EDGE,"E4.0.4.1");var subQ1=sQuery(id+"F0.wireOp",EDGE,"E1.left");var subQ2=makeQuery(id+"F0.imprint","INTERSECT",VERTEX,{"derivedFrom":[subQ1,subQ0]});Q40=makeQuery(id+"F0.imprint","IMPRINT",FACE,{"disambiguationData":[TD([[makeQuery(id+"F0.imprint","IMPRINT",EDGE,{"disambiguationData":[TD([[subQ2,-1.0]])],"derivedFrom":subQ1}),1.0]])]});}
            var Q41;
            {var subQ5=sQuery(id+"F0.wireOp",EDGE,"E4.0.4.3");Q41=makeQuery(id+"F0.imprint","IMPRINT",FACE,{"disambiguationData":[TD([[makeQuery(id+"F0.imprint","IMPRINT",EDGE,{"derivedFrom":subQ5}),-1.0]])]});}
            var Q42;
            {var subQ0=sQuery(id+"F0.wireOp",EDGE,"E4.0.3.1");var subQ1=sQuery(id+"F0.wireOp",EDGE,"E1.left");var subQ2=makeQuery(id+"F0.imprint","INTERSECT",VERTEX,{"derivedFrom":[subQ1,subQ0]});Q42=makeQuery(id+"F0.imprint","IMPRINT",FACE,{"disambiguationData":[TD([[makeQuery(id+"F0.imprint","IMPRINT",EDGE,{"disambiguationData":[TD([[subQ2,-1.0]])],"derivedFrom":subQ1}),1.0]])]});}
            var Q43;
            {var subQ5=sQuery(id+"F0.wireOp",EDGE,"E4.0.3.3");Q43=makeQuery(id+"F0.imprint","IMPRINT",FACE,{"disambiguationData":[TD([[makeQuery(id+"F0.imprint","IMPRINT",EDGE,{"derivedFrom":subQ5}),-1.0]])]});}
            var Q44;
            {var subQ0=sQuery(id+"F0.wireOp",EDGE,"E4.0.2.1");var subQ1=sQuery(id+"F0.wireOp",EDGE,"E1.left");var subQ2=makeQuery(id+"F0.imprint","INTERSECT",VERTEX,{"derivedFrom":[subQ1,subQ0]});Q44=makeQuery(id+"F0.imprint","IMPRINT",FACE,{"disambiguationData":[TD([[makeQuery(id+"F0.imprint","IMPRINT",EDGE,{"disambiguationData":[TD([[subQ2,-1.0]])],"derivedFrom":subQ1}),1.0]])]});}
            var Q45;
            {var subQ5=sQuery(id+"F0.wireOp",EDGE,"E4.0.2.3");Q45=makeQuery(id+"F0.imprint","IMPRINT",FACE,{"disambiguationData":[TD([[makeQuery(id+"F0.imprint","IMPRINT",EDGE,{"derivedFrom":subQ5}),-1.0]])]});}
            var Q46;
            {var subQ0=sQuery(id+"F0.wireOp",EDGE,"E4.0.1.1");var subQ1=sQuery(id+"F0.wireOp",EDGE,"E1.left");var subQ2=makeQuery(id+"F0.imprint","INTERSECT",VERTEX,{"derivedFrom":[subQ1,subQ0]});Q46=makeQuery(id+"F0.imprint","IMPRINT",FACE,{"disambiguationData":[TD([[makeQuery(id+"F0.imprint","IMPRINT",EDGE,{"disambiguationData":[TD([[subQ2,-1.0]])],"derivedFrom":subQ1}),1.0]])]});}
            var Q47;
            {var subQ5=sQuery(id+"F0.wireOp",EDGE,"E4.0.1.3");Q47=makeQuery(id+"F0.imprint","IMPRINT",FACE,{"disambiguationData":[TD([[makeQuery(id+"F0.imprint","IMPRINT",EDGE,{"derivedFrom":subQ5}),-1.0]])]});}
            var Q48;
            {var subQ0=sQuery(id+"F0.wireOp",EDGE,"E3.bottom");var subQ1=sQuery(id+"F0.wireOp",EDGE,"E1.left");var subQ2=makeQuery(id+"F0.imprint","INTERSECT",VERTEX,{"derivedFrom":[subQ1,subQ0]});Q48=makeQuery(id+"F0.imprint","IMPRINT",FACE,{"disambiguationData":[TD([[makeQuery(id+"F0.imprint","IMPRINT",EDGE,{"disambiguationData":[TD([[subQ2,-1.0]])],"derivedFrom":subQ1}),1.0]])]});}
            var Q49;
            {var subQ5=sQuery(id+"F0.wireOp",EDGE,"E3.right");Q49=makeQuery(id+"F0.imprint","IMPRINT",FACE,{"disambiguationData":[TD([[makeQuery(id+"F0.imprint","IMPRINT",EDGE,{"derivedFrom":subQ5}),-1.0]])]});}
            extrude(context, id + "F2", {"entities" : qUnion([Q0, Q1, Q2, Q3, Q4, Q5, Q6, Q7, Q8, Q9, Q10, Q11, Q12, Q13, Q14, Q15, Q16, Q17, Q18, Q19, Q20, Q21, Q22, Q23, Q24, Q25, Q26, Q27, Q28, Q29, Q30, Q31, Q32, Q33, Q34, Q35, Q36, Q37, Q38, Q39, Q40, Q41, Q42, Q43, Q44, Q45, Q46, Q47, Q48, Q49]), "oppositeDirection" : true, "depth" : 38.1 * mm});
        }
    });
